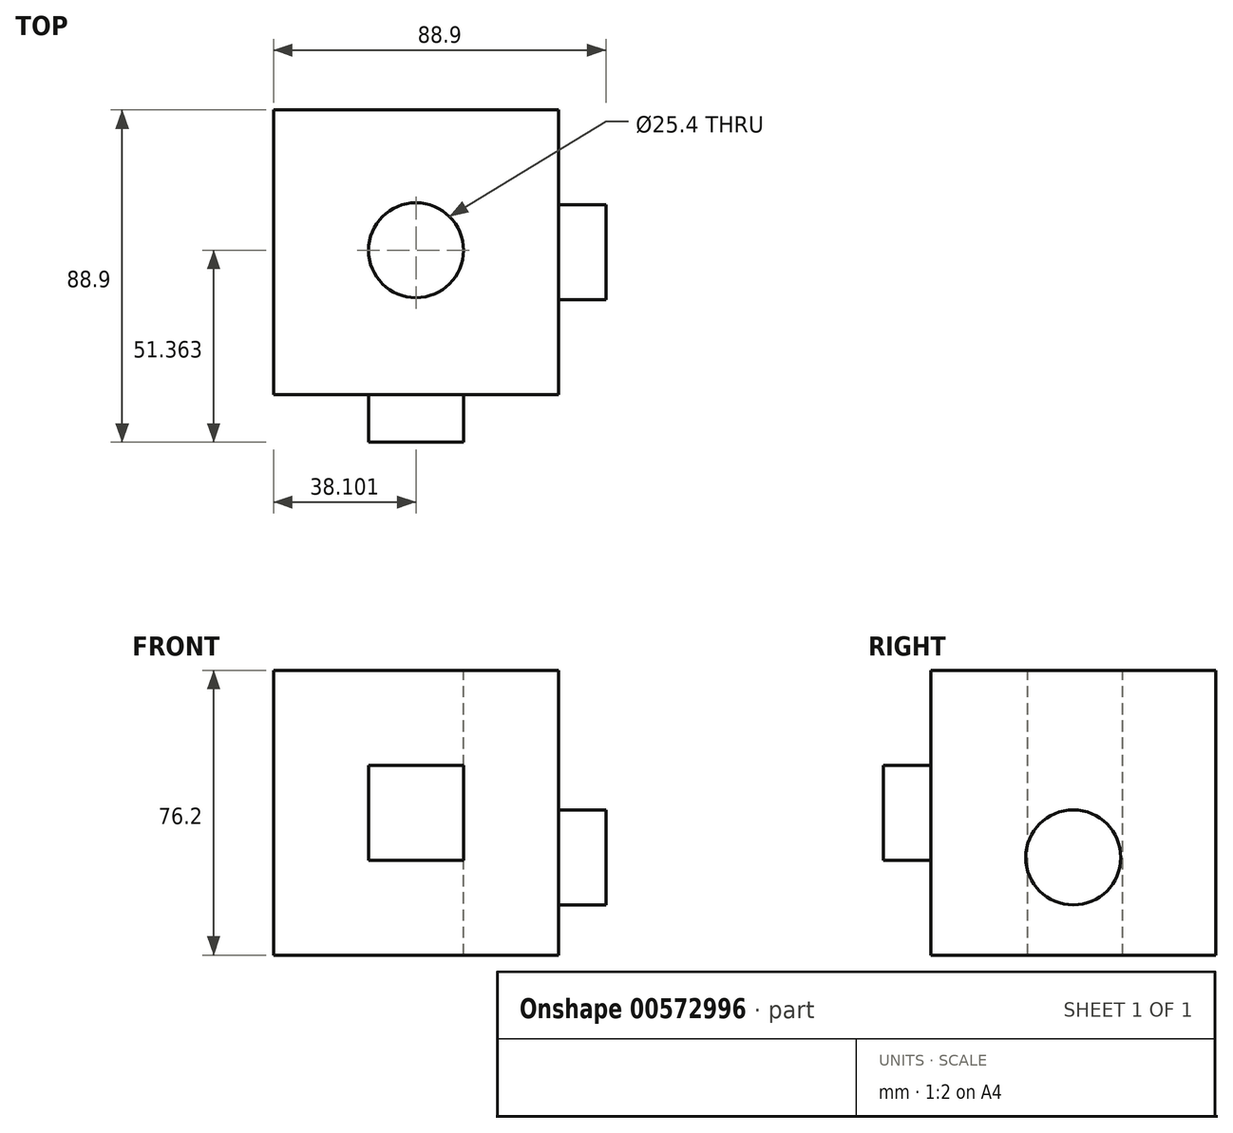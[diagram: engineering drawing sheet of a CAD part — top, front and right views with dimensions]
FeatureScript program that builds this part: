
annotation { "Feature Type Name" : "Feature", "Feature Type Description" : "" }
export const myFeature = defineFeature(function(context is Context, id is Id, definition is map)
    precondition{}
    {
        {
            var Q0;
            Q0=qCreatedBy(makeId("Front.planeOp"),FACE);
            var sketch = newSketch(context, id + "F0", { "sketchPlane" : qUnion([Q0])});
            skLineSegment(sketch, "E0.bottom", {"start": v(-39.33, 17.7) * mm, "end": v(36.87, 17.7) * mm});
            skLineSegment(sketch, "E0.top", {"start": v(-39.33, 93.9) * mm, "end": v(36.87, 93.9) * mm});
            skLineSegment(sketch, "E0.left", {"start": v(-39.33, 17.7) * mm, "end": v(-39.33, 93.9) * mm});
            skLineSegment(sketch, "E0.right", {"start": v(36.87, 17.7) * mm, "end": v(36.87, 93.9) * mm});
            skPoint(sketch, "E1.oppositeSnap0", {"position": v(-1.23, 17.7) * mm});
            skLineSegment(sketch, "E1.left", {"start": v(0, 17.7) * mm, "end": v(0, 17.7) * mm});
            skLineSegment(sketch, "E1.right", {"start": v(-81.25, 17.7) * mm, "end": v(-81.25, 17.7) * mm});
            skSolve(sketch);
        }
        {
            var Q0;
            Q0=makeQuery(id+"F0.imprint","IMPRINT",FACE,{"disambiguationData":[TD([[makeQuery(id+"F0.imprint","IMPRINT",EDGE,{"derivedFrom":sQuery(id+"F0.wireOp",EDGE,"E0.bottom")}),1.0]])]});
            extrude(context, id + "F1", {"entities" : qUnion([Q0]), "depth" : 76.2 * mm, "offsetDistance" : 25.4 * mm});
        }
        {
            var Q0;
            Q0=makeQuery(id+"F1.opExtrude","CAP_FACE",FACE,{"disambiguationData":[OSD([sQuery(id+"F0.wireOp",EDGE,"E0.bottom"),sQuery(id+"F0.wireOp",EDGE,"E0.top"),sQuery(id+"F0.wireOp",EDGE,"E0.left"),sQuery(id+"F0.wireOp",EDGE,"E0.right")])],"isStart":false});
            var sketch = newSketch(context, id + "F2", { "sketchPlane" : qUnion([Q0])});
            skLineSegment(sketch, "E2.bottom", {"start": v(-13.93, 68.5) * mm, "end": v(11.47, 68.5) * mm});
            skLineSegment(sketch, "E2.top", {"start": v(-13.93, 43.1) * mm, "end": v(11.47, 43.1) * mm});
            skLineSegment(sketch, "E2.left", {"start": v(-13.93, 68.5) * mm, "end": v(-13.93, 43.1) * mm});
            skLineSegment(sketch, "E2.right", {"start": v(11.47, 68.5) * mm, "end": v(11.47, 43.1) * mm});
            skSolve(sketch);
        }
        {
            var Q0;
            Q0=makeQuery(id+"F2.imprint","IMPRINT",FACE,{"disambiguationData":[TD([[makeQuery(id+"F2.imprint","IMPRINT",EDGE,{"derivedFrom":sQuery(id+"F2.wireOp",EDGE,"E2.bottom")}),-1.0]])]});
            extrude(context, id + "F3", {"entities" : qUnion([Q0]), "operationType" : NewBodyOperationType.ADD, "depth" : 12.7 * mm, "offsetDistance" : 25.4 * mm});
        }
        {
            var Q0;
            Q0=makeQuery(id+"F1.opExtrude","SWEPT_FACE",FACE,{"disambiguationData":[OSD([sQuery(id+"F0.wireOp",EDGE,"E0.right")])]});
            var sketch = newSketch(context, id + "F4", { "sketchPlane" : qUnion([Q0])});
            skCircle(sketch, "E3", {"center": v(-38.1, 43.82) * mm, "radius": 12.7 * mm});
            skSolve(sketch);
        }
        {
            var Q0;
            Q0=makeQuery(id+"F4.imprint","IMPRINT",FACE,{"disambiguationData":[TD([[makeQuery(id+"F4.imprint","IMPRINT",EDGE,{"derivedFrom":sQuery(id+"F4.wireOp",EDGE,"E3")}),1.0]])]});
            extrude(context, id + "F5", {"entities" : qUnion([Q0]), "operationType" : NewBodyOperationType.ADD, "depth" : 12.7 * mm, "offsetDistance" : 25.4 * mm});
        }
        {
            var Q0;
            Q0=makeQuery(id+"F1.opExtrude","SWEPT_FACE",FACE,{"disambiguationData":[OSD([sQuery(id+"F0.wireOp",EDGE,"E0.top")])]});
            var sketch = newSketch(context, id + "F6", { "sketchPlane" : qUnion([Q0])});
            skPoint(sketch, "E4", {"position": v(-1.23, -37.54) * mm});
            skSolve(sketch);
        }
        {
            var Q0;
            Q0=sQuery(id+"F6.wireOp",VERTEX,"E4");
            var Q1;
            Q1=makeQuery(id+"F1.opExtrude","SWEPT_BODY",BODY,{"disambiguationData":[OSD([sQuery(id+"F0.wireOp",EDGE,"E0.bottom"),sQuery(id+"F0.wireOp",EDGE,"E0.top"),sQuery(id+"F0.wireOp",EDGE,"E0.left"),sQuery(id+"F0.wireOp",EDGE,"E0.right")])]});
            hole(context, id + "F7", {"style" : HoleStyle.SIMPLE, "endStyle" : HoleEndStyle.THROUGH, "holeDiameter" : 25.4 * mm, "isTappedThrough" : true, "tappedDepth" : 12.7 * mm, "tapClearance" : 3, "locations" : qUnion([Q0]), "scope" : qUnion([Q1])});
        }
    });
